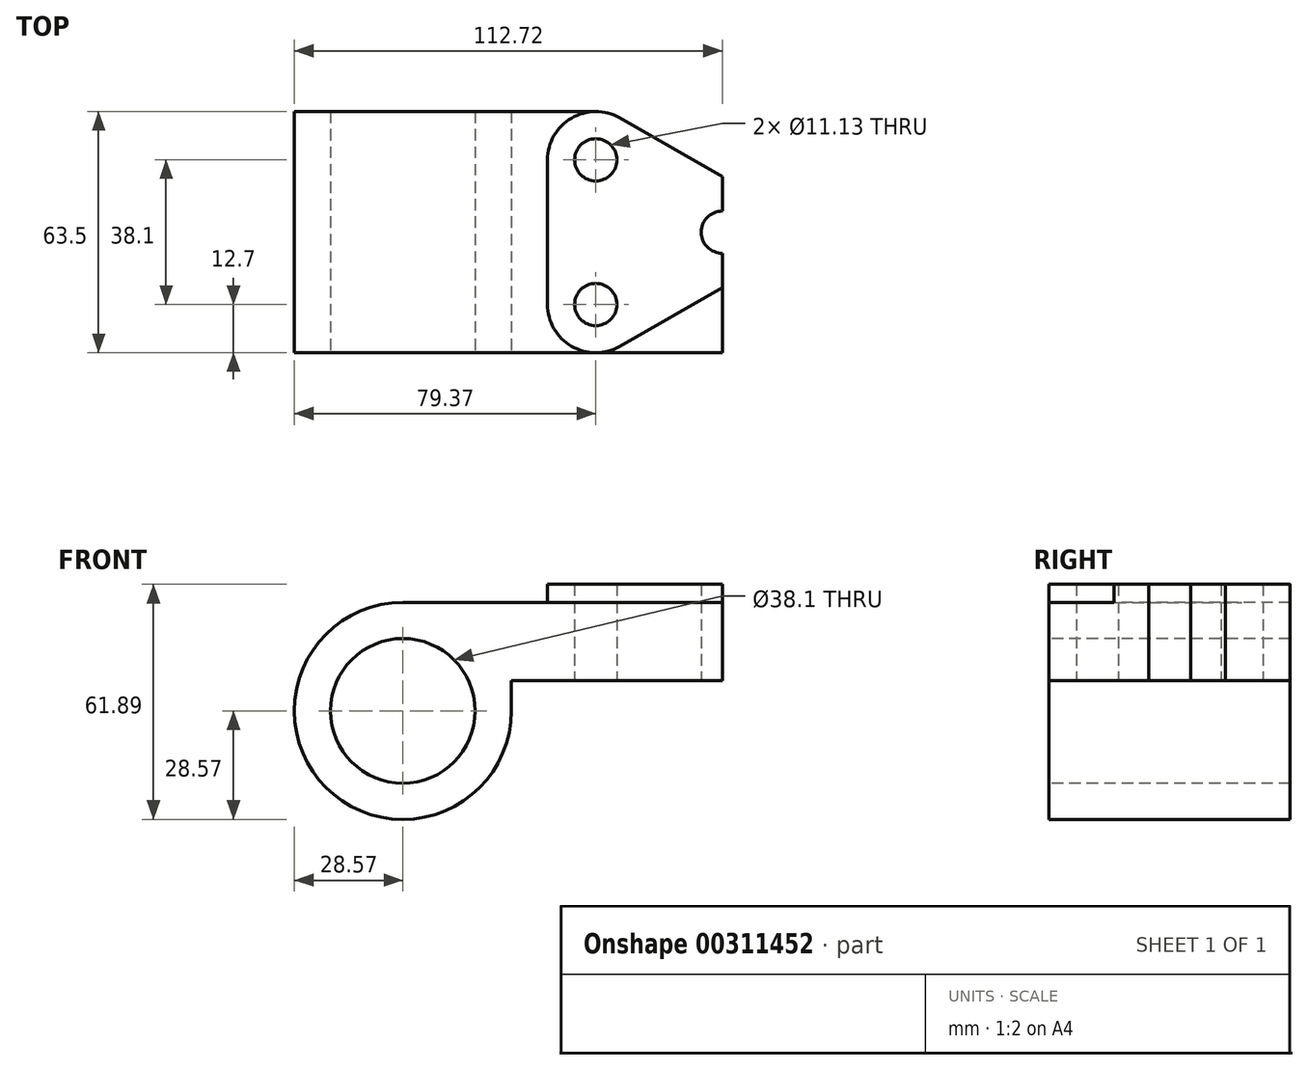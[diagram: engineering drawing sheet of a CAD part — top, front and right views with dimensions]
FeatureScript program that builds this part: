
annotation { "Feature Type Name" : "Feature", "Feature Type Description" : "" }
export const myFeature = defineFeature(function(context is Context, id is Id, definition is map)
    precondition{}
    {
        {
            var Q0;
            Q0=qCreatedBy(makeId("Front.planeOp"),FACE);
            var sketch = newSketch(context, id + "F0", { "sketchPlane" : qUnion([Q0])});
            skCircle(sketch, "E0", {"center": v(0, 0) * mm, "radius": 19.05 * mm});
            skArc(sketch, "E1", {"start": v(0, 28.58) * mm, "mid": v(-28.58, 0) * mm, "end": v(0, -28.58) * mm});
            skLineSegment(sketch, "E2", {"start": v(84.15, 28.58) * mm, "end": v(0, 28.58) * mm});
            skLineSegment(sketch, "E3", {"start": v(0, -28.58) * mm, "end": v(84.15, -28.58) * mm});
            skLineSegment(sketch, "E4", {"start": v(84.15, 28.58) * mm, "end": v(84.15, -28.58) * mm});
            skSolve(sketch);
        }
        {
            var Q0;
            Q0 = qSketchRegion(id + "F0", true);
            extrude(context, id + "F1", {"entities" : qUnion([Q0]), "oppositeDirection" : true, "depth" : 63.5 * mm});
        }
        {
            var Q0;
            Q0=qCreatedBy(makeId("Front.planeOp"),FACE);
            var sketch = newSketch(context, id + "F2", { "sketchPlane" : qUnion([Q0])});
            skLineSegment(sketch, "E5.bottom", {"start": v(84.15, -28.57) * mm, "end": v(33.35, -28.58) * mm});
            skLineSegment(sketch, "E5.top", {"start": v(84.15, 7.92) * mm, "end": v(33.35, 7.92) * mm});
            skLineSegment(sketch, "E5.left", {"start": v(84.15, -28.57) * mm, "end": v(84.15, 7.92) * mm});
            skLineSegment(sketch, "E5.right", {"start": v(33.35, -28.58) * mm, "end": v(33.35, 7.92) * mm});
            skSolve(sketch);
        }
        {
            var Q0;
            Q0 = qSketchRegion(id + "F2", true);
            extrude(context, id + "F3", {"entities" : qUnion([Q0]), "operationType" : NewBodyOperationType.REMOVE, "endBound" : BoundingType.THROUGH_ALL, "oppositeDirection" : true, "depth" : 25.4 * mm});
        }
        {
            var Q0;
            Q0=qCreatedBy(makeId("Front.planeOp"),FACE);
            var sketch = newSketch(context, id + "F4", { "sketchPlane" : qUnion([Q0])});
            skArc(sketch, "E6", {"start": v(0, -28.58) * mm, "mid": v(20.2, -20.2) * mm, "end": v(28.58, 0) * mm});
            skLineSegment(sketch, "E7", {"start": v(28.58, 0) * mm, "end": v(28.58, 7.92) * mm});
            skLineSegment(sketch, "E8", {"start": v(28.58, 7.92) * mm, "end": v(52.32, 7.92) * mm});
            skLineSegment(sketch, "E9", {"start": v(0, -28.58) * mm, "end": v(33.35, -28.57) * mm});
            skLineSegment(sketch, "E10", {"start": v(33.35, -28.58) * mm, "end": v(33.35, 7.92) * mm});
            skSolve(sketch);
        }
        {
            var Q0;
            Q0=makeQuery(id+"F4.imprint","IMPRINT",FACE,{"disambiguationData":[TD([[makeQuery(id+"F4.imprint","IMPRINT",EDGE,{"derivedFrom":sQuery(id+"F4.wireOp",EDGE,"E6")}),-1.0]])]});
            extrude(context, id + "F5", {"entities" : qUnion([Q0]), "operationType" : NewBodyOperationType.REMOVE, "endBound" : BoundingType.THROUGH_ALL, "oppositeDirection" : true, "depth" : 25.4 * mm});
        }
        {
            var Q0;
            Q0=makeQuery(id+"F5.boolean.opBoolean","MERGE",FACE,{"derivedFrom":[makeQuery(id+"F3.boolean.opBoolean","COPY",FACE,{"derivedFrom":makeQuery(id+"F3.opExtrude","SWEPT_FACE",FACE,{"disambiguationData":[OSD([sQuery(id+"F2.wireOp",EDGE,"E5.top")])]})}),makeQuery(id+"F5.opExtrude","SWEPT_FACE",FACE,{"disambiguationData":[OSD([sQuery(id+"F4.wireOp",EDGE,"E8")])]})]});
            var sketch = newSketch(context, id + "F6", { "sketchPlane" : qUnion([Q0])});
            skCircle(sketch, "E11", {"center": v(50.8, -12.7) * mm, "radius": 5.56 * mm});
            skCircle(sketch, "E12", {"center": v(50.8, -50.8) * mm, "radius": 5.56 * mm});
            skCircle(sketch, "E13", {"center": v(84.15, -31.75) * mm, "radius": 5.56 * mm});
            skLineSegment(sketch, "E14", {"start": v(38.1, -50.8) * mm, "end": v(38.1, -12.7) * mm});
            skArc(sketch, "E15", {"start": v(38.1, -12.7) * mm, "mid": v(44.42, -1.72) * mm, "end": v(57.1, -1.67) * mm});
            skArc(sketch, "E16", {"start": v(38.1, -50.8) * mm, "mid": v(44.42, -61.78) * mm, "end": v(57.1, -61.83) * mm});
            skLineSegment(sketch, "E17", {"start": v(57.1, -1.67) * mm, "end": v(90.45, -20.72) * mm});
            skLineSegment(sketch, "E18", {"start": v(57.1, -61.83) * mm, "end": v(90.45, -42.78) * mm});
            skArc(sketch, "E19", {"start": v(90.45, -20.72) * mm, "mid": v(96.85, -31.75) * mm, "end": v(90.45, -42.78) * mm});
            skSolve(sketch);
        }
        {
            var Q0;
            Q0=makeQuery(id+"F6.imprint","IMPRINT",FACE,{"disambiguationData":[TD([[makeQuery(id+"F6.imprint","IMPRINT",EDGE,{"derivedFrom":sQuery(id+"F6.wireOp",EDGE,"E11")}),-1.0]])]});
            var Q1;
            {var subQ0=sQuery(id+"F6.wireOp",EDGE,"E19");Q1=makeQuery(id+"F6.imprint","IMPRINT",FACE,{"disambiguationData":[TD([[makeQuery(id+"F6.imprint","IMPRINT",EDGE,{"derivedFrom":subQ0}),-1.0]])]});}
            extrude(context, id + "F7", {"entities" : qUnion([Q0, Q1]), "operationType" : NewBodyOperationType.ADD, "oppositeDirection" : true, "depth" : 20.65 * mm});
        }
        {
            var Q0;
            Q0=makeQuery(id+"F6.imprint","IMPRINT",FACE,{"disambiguationData":[TD([[makeQuery(id+"F6.imprint","IMPRINT",EDGE,{"derivedFrom":sQuery(id+"F6.wireOp",EDGE,"E11")}),1.0]])]});
            var Q1;
            Q1=makeQuery(id+"F6.imprint","IMPRINT",FACE,{"disambiguationData":[TD([[makeQuery(id+"F6.imprint","IMPRINT",EDGE,{"derivedFrom":sQuery(id+"F6.wireOp",EDGE,"E12")}),1.0]])]});
            var Q2;
            {var subQ0=sQuery(id+"F6.wireOp",EDGE,"E13");var subQ1=makeQuery(id+"F3.boolean.opBoolean","COPY",EDGE,{"derivedFrom":makeQuery(id+"F3.opExtrude","SWEPT_EDGE",EDGE,{"disambiguationData":[OSD([sQuery(id+"F2.wireOp",EDGE,"E5.top"),sQuery(id+"F2.wireOp",EDGE,"E5.left")])]})});var subQ2=makeQuery(id+"F6.imprint","INTERSECT",VERTEX,{"disambiguationData":[OD(0.0)],"derivedFrom":[subQ1,subQ0]});Q2=makeQuery(id+"F6.imprint","IMPRINT",FACE,{"disambiguationData":[TD([[makeQuery(id+"F6.imprint","IMPRINT",EDGE,{"disambiguationData":[TD([[subQ2,-1.0]])],"derivedFrom":subQ0}),1.0]])]});}
            var Q3;
            Q3=sQuery(id+"F6.wireOp",EDGE,"E11");
            var Q4;
            Q4=sQuery(id+"F6.wireOp",EDGE,"E12");
            var Q5;
            Q5=sQuery(id+"F6.wireOp",EDGE,"E13");
            extrude(context, id + "F8", {"entities" : qUnion([Q0, Q1, Q2]), "operationType" : NewBodyOperationType.REMOVE, "surfaceEntities" : qUnion([Q3, Q4, Q5]), "endBound" : BoundingType.THROUGH_ALL, "oppositeDirection" : true, "depth" : 25.4 * mm});
        }
        {
            var Q0;
            {var subQ0=sQuery(id+"F6.wireOp",EDGE,"E17");var subQ1=sQuery(id+"F6.wireOp",EDGE,"E15");var subQ2=makeQuery(id+"F6.imprint","INTERSECT",VERTEX,{"derivedFrom":[subQ1,subQ0]});Q0=makeQuery(id+"F6.imprint","IMPRINT",FACE,{"disambiguationData":[TD([[makeQuery(id+"F6.imprint","IMPRINT",EDGE,{"disambiguationData":[TD([[subQ2,1.0]])],"derivedFrom":subQ1}),1.0]])]});}
            var Q1;
            {var subQ0=sQuery(id+"F6.wireOp",EDGE,"E18");var subQ1=sQuery(id+"F6.wireOp",EDGE,"E16");var subQ2=makeQuery(id+"F6.imprint","INTERSECT",VERTEX,{"derivedFrom":[subQ1,subQ0]});Q1=makeQuery(id+"F6.imprint","IMPRINT",FACE,{"disambiguationData":[TD([[makeQuery(id+"F6.imprint","IMPRINT",EDGE,{"disambiguationData":[TD([[subQ2,-1.0]])],"derivedFrom":subQ0}),-1.0]])]});}
            extrude(context, id + "F9", {"entities" : qUnion([Q0, Q1]), "operationType" : NewBodyOperationType.REMOVE, "oppositeDirection" : true, "depth" : 25.4 * mm});
        }
        {
            var Q0;
            Q0=makeQuery(id+"F6.imprint","IMPRINT",FACE,{"disambiguationData":[TD([[makeQuery(id+"F6.imprint","IMPRINT",EDGE,{"derivedFrom":sQuery(id+"F6.wireOp",EDGE,"E11")}),-1.0]])]});
            var Q1;
            {var subQ0=sQuery(id+"F6.wireOp",EDGE,"E19");Q1=makeQuery(id+"F6.imprint","IMPRINT",FACE,{"disambiguationData":[TD([[makeQuery(id+"F6.imprint","IMPRINT",EDGE,{"derivedFrom":subQ0}),-1.0]])]});}
            extrude(context, id + "F10", {"entities" : qUnion([Q0, Q1]), "operationType" : NewBodyOperationType.ADD, "oppositeDirection" : true, "depth" : 25.4 * mm});
        }
    });
